# Revit family: ADB Electric range cookers L600
name_source: partatom
category: Equipement spécialisé
units: mm (PartAtom-declared; Revit-internal decimal feet)

## family parameters
Basée sur le plan de construction = Non
Conserver l'orientation des annotations = Non
Cote de connecteur circulaire = Utiliser le diamètre
Couper avec des vides une fois chargée = Non
Numéro OmniClass = 23.40.40.14.17.11
Partagée = Non
Repère de localisation dans la pièce = Non
Titre OmniClass = Cookers, Ovens, Stoves
Toujours verticalement = Oui
Type d'élément = Normal

## types (1)
- 4 Electric hotplates, 1 oven - CE 641 E
    B = 180 mm  [stored 0.590551 ft]
    C = 410 mm  [stored 1.34514 ft]
    Commentaires du type = Ambassade range - Electric range cookers
    Description = Electric range cooker 4 Electric hotplates, 1 oven - CE 641 E
    Elévation par défaut = 0 mm  [stored 0 ft]
    Fabricant = Société Industrielle de Lacanche
    Modèle = CE 641 E
    Pbase = 9500 W
    Table = CE641E _4 plaques électriques
    URL = https://www.ambassade-de-bourgogne.com
    Weight = 84.00 kg

note: [stored X ft] marks values corroborated as IEEE doubles in the binary element streams (Revit-internal decimal feet)
